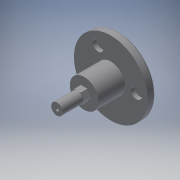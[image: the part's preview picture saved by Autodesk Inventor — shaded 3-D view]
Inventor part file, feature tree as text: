
AUTODESK INVENTOR PART (.ipt)
format: ipt  version: 2019 (Build 230136000, 136)  size: 239,104 bytes
history: native  units: in
note: dims shown in document units (in); Inventor stores cm internally (conversion verified against a paired STEP export)
features: extrude x9, sketch x9, fillet x1, pattern_circular x1
ambient origin geometry x8: Origin, YZ Plane, XZ Plane, XY Plane, X Axis, Y Axis, Z Axis, Center Point
bodies: Solid1 (feature_tree)
feature tree (20):
  extrude  "Extrusion1"  Depth=0.6in TaperAngle=0.0deg
  extrude  "Extrusion2"  Depth=1.3in TaperAngle=0.0deg
  extrude  "Extrusion3"  Depth=0.555in TaperAngle=0.0deg
  extrude  "Extrusion4"  Depth=1.0in TaperAngle=0.0deg
  extrude  "Extrusion5"  Depth=1.0in TaperAngle=0.0deg
  extrude  "Extrusion6"  Depth=0.2in TaperAngle=0.0deg
  extrude  "Extrusion7"  Depth=0.6in
  fillet  "Fillet1"  Radius=0.6in
  extrude  "Extrusion8"  Depth=1.175in
  extrude  "Extrusion9"  Depth=0.2in TaperAngle=0.0deg
  pattern_circular  "Circular Pattern1"  Count=3 Angle=360.0deg
  sketch  "Sketch1"  dims[d0=3.6in d1=0.6in d2=0.0in]
  sketch  "Sketch2"  dims[d3=1.4in d4=1.3in d5=0.0in]
  sketch  "Sketch3"  dims[d6=0.555in d7=0.33in d8=0.0in]
  sketch  "Sketch4"  dims[d9=0.56in d10=1.0in d11=0.0in]
  sketch  "Sketch5"  dims[d12=0.19in d13=1.0in d14=0.0in]
  sketch  "Sketch6"  dims[d15=2.0in d16=0.2in d17=0.0in]
  sketch  "Sketch7"  dims[d18=0.125in d19=1.35in d20=0.6in d21=0.0in]
  sketch  "Sketch8"  dims[d22=1.175in d23=0.0in d24=0.55in]
  sketch  "Sketch9"  dims[d25=0.55in d26=0.2in d27=0.0in d28=1.1811in d29=360.0deg]
